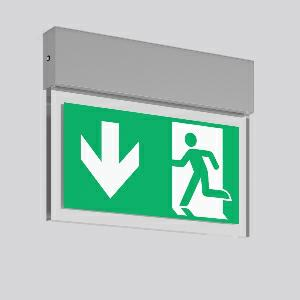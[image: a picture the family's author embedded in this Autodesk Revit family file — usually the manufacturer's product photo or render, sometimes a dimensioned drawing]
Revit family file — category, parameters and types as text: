
# Revit family: halyxx_671744_004_1_07_28de
name_source: partatom
category: Lighting Fixtures
units: mm (PartAtom-declared; Revit-internal decimal feet)

## family parameters
Cut with Voids When Loaded = No
Host = Face
Light Source = No
Part Type = Normal
Room Calculation Point = No
Round Connector Dimension = Use Diameter
Shared = No

## types (1)
- HALYXX (1 x LED Modul 840, 95 lm, 4000)
    Apparent Load = 4 VA
    Approval mark = CE
    CIE Flux Codes = 18 45 74 52 100
    Color Rendering = 80
    Color Temperature = 4000
    Default Elevation = 1800 mm
    Description = Series: HALYXX
Luminaire for escape route identification. Housing: extruded aluminium profile, anodised or powder-coated. Display panel: highly transparent panel, plastic, with legend on one side/both sides. Electronic ballast included. Self-contained system with automatic self-test and feedback via DALI bus, only to RZB DALI monitoring system. Please indicate legend number when placing your order! 
Colour: anodised aluminium
Length: 340 mm
Width: 40 mm
Height: 270 mm
Weight: 2.18 kg
Operating mode: maintained power mode
Viewing Distance: 30 m
Duration time: 3 h
Lamp: LED
Socket: without socket
Colour temperature: 4000K
Colour rendering index (CRI): 80
System power: 4.2 W
Rated luminous flux: 95 lm
Luminous flux, emergency: 25
System power, emergency: -
Control gear: Electronic transformer
Protection class: I
Type of protection: IP 40
    Height = 270 mm
    Lamp = 1 x LED Modul 840
    Lamp Light Flux = 95 lm
    Lamp count = 1
    Length = 340 mm
    Lifetime = 50000 h
    Luminous efficacy = 23 lm/W
    Manufacturer = RZB
    ModVariant = No
    Model = 671744.004.1.07
    Mounting Place = Ceiling
    Mounting Type = Surface mounted
    Number of Poles = 1
    OnlyDefault = Yes
    Power Factor = 1
    Product Name = HALYXX
    Product group = Surface mounted ceiling luminaires
    ProductGroupID = 303
    Protection Class = Protection class I
    Protection Degree = IP 40
    RLX_Detail_Level = 1
    RLX_Emergency_Light_Flux = 25 lm
    RLX_Emergency_Type = 3
    RLX_Emergency_Type_DB = Yes
    RlxData = <blob elided: 55033 chars, md5=e21ae612>
    Socket = socket
    Standby Power = 0 W
    System Light Flux = 95 lm
    System Power = 4 W
    Type Comments = Product without accessories
    Type Image = 671744.004.jpg
    URL = http://relux.com
    VarID = ---
    Voltage = 230 V
    Voltage Range = 220-240 V
    Weight = 0.00 kg
    Width = 40 mm  [stored 0.131234 ft]

note: [stored X ft] marks values corroborated as IEEE doubles in the binary element streams (Revit-internal decimal feet)

## geometry (parser evidence)
native form markers: Blend x4, Sweep x12
no freeform markers — native parametric forms only
